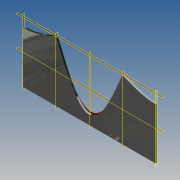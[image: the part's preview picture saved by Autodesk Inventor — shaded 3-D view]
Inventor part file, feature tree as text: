
AUTODESK INVENTOR PART (.ipt)
format: ipt  version: 2017.3 (Build 213257000, 257)  size: 194,048 bytes
history: native  units: in
note: dims shown in document units (in); Inventor stores cm internally (conversion verified against a paired STEP export)
features: plane x7, extrude x2, sketch x2, other x2
ambient origin geometry x8: Origin, YZ Plane, XZ Plane, XY Plane, X Axis, Y Axis, Z Axis, Center Point
bodies: Solid1 (feature_tree)
feature tree (13):
  extrude  "Extrusion1"  Depth=1.5in TaperAngle=0.0deg
  extrude  "Extrusion2"  Depth=0.001in TaperAngle=0.0deg
  plane  "Work Plane1 Centerline at surface"
  plane  "Work Plane2 Centerline at centerline"
  plane  "Work Plane3 Top"
  plane  "Work Plane4 Right"
  plane  "Work Plane5 Bottom"
  plane  "Work Plane6 Left"
  plane  "Work Plane7 Top"
  sketch  "Sketch1"  dims[d0=0.0in d1=46.0713in d2=1.5in d3=0.0in]
  other  "2D Equation Curve1"
  sketch  "Sketch2"  dims[d4=0.0in d5=46.0713in d6=0.001in d7=0.0in d8=-26.6245in d9=-52.9642in d10=0.0in d11=-29.2553in d12=-58.5106in d13=-87.7659in d14=0.0in]
  other  "2D Equation Curve2"
